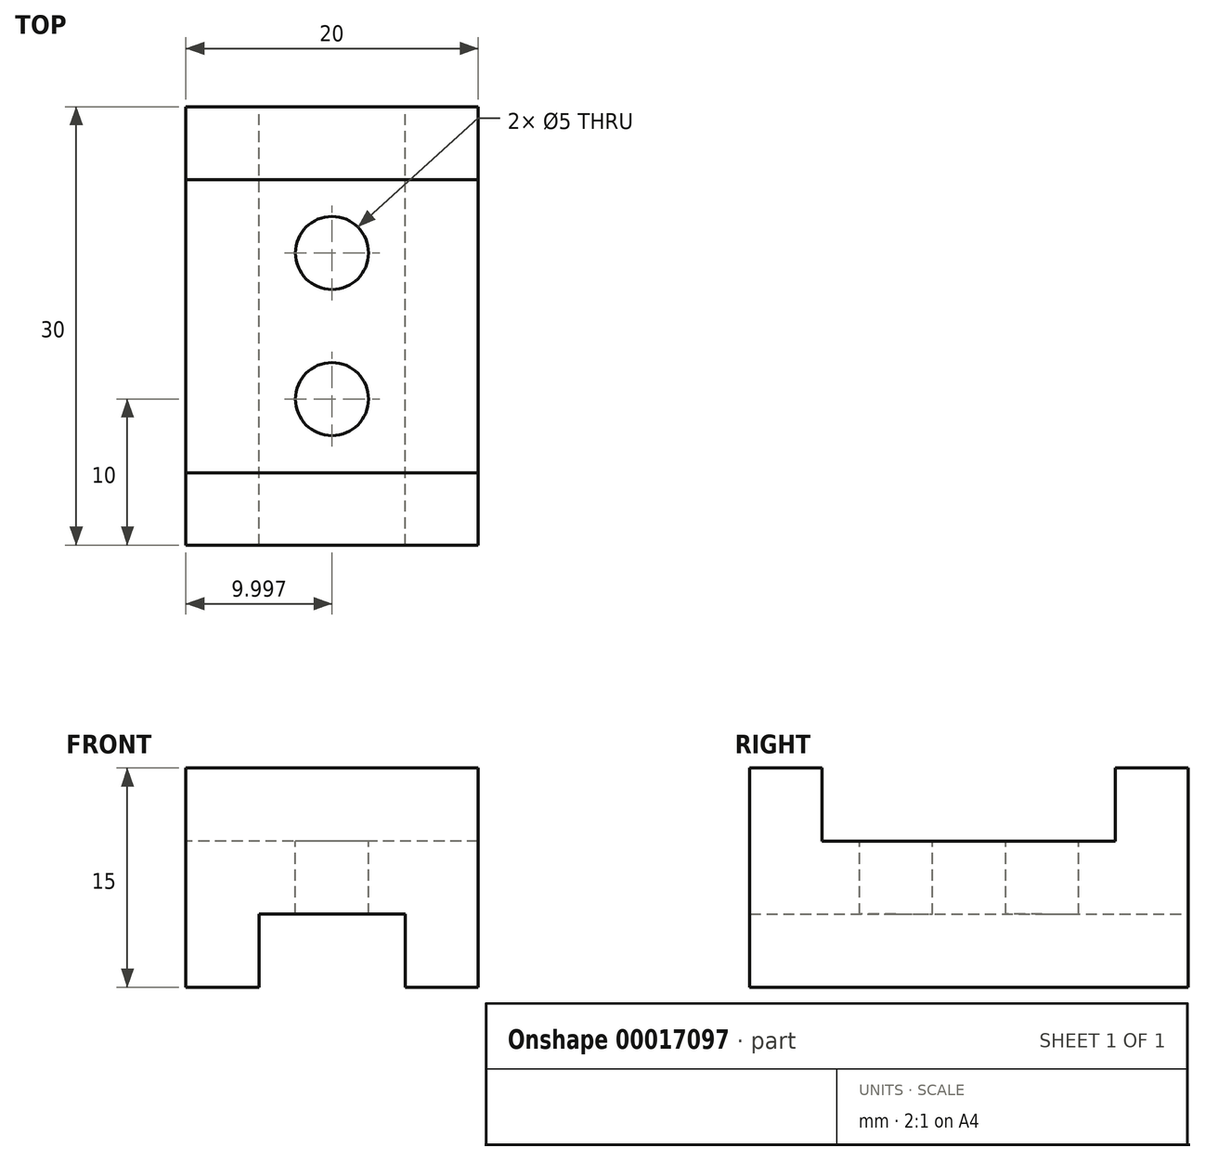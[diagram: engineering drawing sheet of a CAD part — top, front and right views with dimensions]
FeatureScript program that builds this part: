
annotation { "Feature Type Name" : "Feature", "Feature Type Description" : "" }
export const myFeature = defineFeature(function(context is Context, id is Id, definition is map)
    precondition{}
    {
        {
            var Q0;
            Q0=qCreatedBy(makeId("Front.planeOp"),FACE);
            var sketch = newSketch(context, id + "F0", { "sketchPlane" : qUnion([Q0])});
            skLineSegment(sketch, "E0", {"start": v(-13.07, 10.92) * mm, "end": v(6.93, 10.92) * mm});
            skLineSegment(sketch, "E1", {"start": v(6.93, 10.92) * mm, "end": v(6.93, -4.08) * mm});
            skLineSegment(sketch, "E2", {"start": v(6.93, -4.08) * mm, "end": v(1.93, -4.08) * mm});
            skLineSegment(sketch, "E3", {"start": v(1.93, -4.08) * mm, "end": v(1.93, 0.92) * mm});
            skLineSegment(sketch, "E4", {"start": v(1.93, 0.92) * mm, "end": v(-8.07, 0.92) * mm});
            skLineSegment(sketch, "E5", {"start": v(-8.07, 0.92) * mm, "end": v(-8.07, -4.08) * mm});
            skLineSegment(sketch, "E6", {"start": v(-8.07, -4.08) * mm, "end": v(-13.07, -4.08) * mm});
            skLineSegment(sketch, "E7", {"start": v(-13.07, -4.08) * mm, "end": v(-13.07, 10.92) * mm});
            skSolve(sketch);
        }
        {
            var Q0;
            Q0=makeQuery(id+"F0.imprint","IMPRINT",FACE,{"disambiguationData":[TD([[makeQuery(id+"F0.imprint","IMPRINT",EDGE,{"derivedFrom":sQuery(id+"F0.wireOp",EDGE,"E0")}),-1.0]])]});
            extrude(context, id + "F1", {"entities" : qUnion([Q0]), "depth" : 30 * mm});
        }
        {
            var Q0;
            Q0=makeQuery(id+"F1.opExtrude","SWEPT_FACE",FACE,{"disambiguationData":[OSD([sQuery(id+"F0.wireOp",EDGE,"E0")])]});
            var sketch = newSketch(context, id + "F2", { "sketchPlane" : qUnion([Q0])});
            skLineSegment(sketch, "E8", {"start": v(6.93, -5) * mm, "end": v(-13.07, -5) * mm});
            skLineSegment(sketch, "E9", {"start": v(6.93, -25.06) * mm, "end": v(-13.07, -25.06) * mm});
            skLineSegment(sketch, "E10", {"start": v(6.93, -5) * mm, "end": v(6.93, -25.06) * mm});
            skLineSegment(sketch, "E11", {"start": v(-13.07, -5) * mm, "end": v(-13.07, -25.06) * mm});
            skSolve(sketch);
        }
        {
            var Q0;
            Q0=makeQuery(id+"F2.imprint","IMPRINT",FACE,{"disambiguationData":[TD([[makeQuery(id+"F2.imprint","IMPRINT",EDGE,{"derivedFrom":sQuery(id+"F2.wireOp",EDGE,"E8")}),1.0]])]});
            extrude(context, id + "F3", {"entities" : qUnion([Q0]), "operationType" : NewBodyOperationType.REMOVE, "oppositeDirection" : true, "depth" : 5 * mm});
        }
        {
            var Q0;
            Q0=makeQuery(id+"F3.boolean.opBoolean","COPY",FACE,{"derivedFrom":makeQuery(id+"F3.opExtrude","CAP_FACE",FACE,{"disambiguationData":[OSD([sQuery(id+"F2.wireOp",EDGE,"E8"),sQuery(id+"F2.wireOp",EDGE,"E9"),sQuery(id+"F2.wireOp",EDGE,"E10"),sQuery(id+"F2.wireOp",EDGE,"E11")])],"isStart":false})});
            var sketch = newSketch(context, id + "F4", { "sketchPlane" : qUnion([Q0])});
            skLineSegment(sketch, "E12", {"start": v(-3.07, -25.06) * mm, "end": v(6.93, -25.06) * mm});
            skLineSegment(sketch, "E13", {"start": v(6.93, -25.06) * mm, "end": v(6.93, -5) * mm});
            skLineSegment(sketch, "E14", {"start": v(6.93, -5) * mm, "end": v(-3.07, -5) * mm});
            skLineSegment(sketch, "E15", {"start": v(-3.07, -5) * mm, "end": v(-13.07, -5) * mm});
            skLineSegment(sketch, "E16", {"start": v(-13.07, -5) * mm, "end": v(-13.07, -25.06) * mm});
            skLineSegment(sketch, "E17", {"start": v(-13.07, -25.06) * mm, "end": v(-3.07, -25.06) * mm});
            skCircle(sketch, "E18", {"center": v(-3.07, -20) * mm, "radius": 2.5 * mm});
            skCircle(sketch, "E19", {"center": v(-3.07, -10) * mm, "radius": 2.5 * mm});
            skSolve(sketch);
        }
        {
            var Q0;
            Q0=makeQuery(id+"F4.imprint","IMPRINT",FACE,{"disambiguationData":[TD([[makeQuery(id+"F4.imprint","IMPRINT",EDGE,{"derivedFrom":sQuery(id+"F4.wireOp",EDGE,"E19")}),1.0]])]});
            var Q1;
            Q1=makeQuery(id+"F4.imprint","IMPRINT",FACE,{"disambiguationData":[TD([[makeQuery(id+"F4.imprint","IMPRINT",EDGE,{"derivedFrom":sQuery(id+"F4.wireOp",EDGE,"E18")}),1.0]])]});
            extrude(context, id + "F5", {"entities" : qUnion([Q0, Q1]), "operationType" : NewBodyOperationType.REMOVE, "endBound" : BoundingType.THROUGH_ALL, "oppositeDirection" : true, "depth" : 25 * mm});
        }
    });
